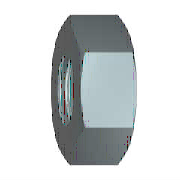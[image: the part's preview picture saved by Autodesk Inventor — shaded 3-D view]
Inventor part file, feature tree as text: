
AUTODESK INVENTOR PART (.ipt)
format: ipt  version: 2013 (Build 170138000, 138)  size: 169,984 bytes
history: native  units: mm (DEFAULTED — no unit token found)
features: sketch x3, chamfer x1, hole x1, other x1, plane x1
ambient origin geometry x7: Origin, YZ Plane, XZ Plane, X Axis, Y Axis, Z Axis, Center Point
bodies: Solid1 (feature_tree), Body (feature_tree)
feature tree (7):
  chamfer  "Chamfer1"  Distance=4.363323mm
  hole  "Thread"  [1 undecoded]
  other  "Work Axis1"
  plane  "Work Plane1"
  sketch  "Sketch1"  dims[d0=6.350853mm]
  sketch  "Sketch2"  dims[d1=2.4mm]
  sketch  "Sketch3"  dims[d2=0.0mm d3=4.363323mm d4=4.363323mm d5=5.5mm d6=5.5mm d7=90.0deg d25=1.221mm d26=6.0mm d27=4.0mm d28=2.0mm d29=14.3117mm d30=8.0mm d31=20.594885mm d8=0.270633mm d9=30.0deg d10=0.270633mm d11=30.0deg d13=0.0mm d14=0.0mm d39=0.0mm d40=0.270633mm d41=0.270633mm d42=0.0mm]
note: 1 required parameter value undecoded (feature->parameter linkage not recoverable at this tier; creation-order binding heuristic only, values carry confidence <= 0.55)
